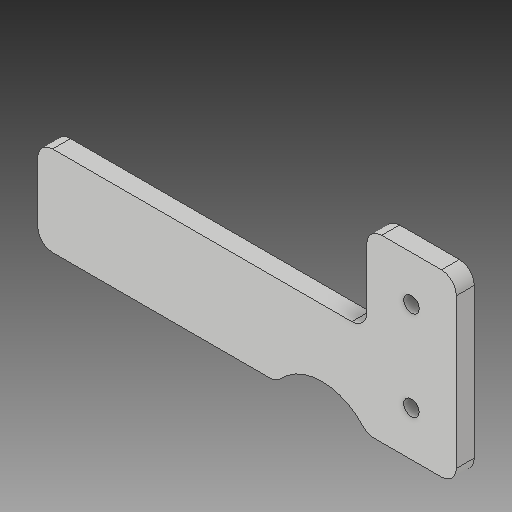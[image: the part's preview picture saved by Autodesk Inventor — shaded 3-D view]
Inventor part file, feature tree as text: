
AUTODESK INVENTOR PART (.ipt)
format: ipt  version: 2018 (Build 220112000, 112)  size: 117,760 bytes
history: native  units: mm
features: other x3, sketch x1
ambient origin geometry x8: Origin, YZ Plane, XZ Plane, XY Plane, X Axis, Y Axis, Z Axis, Center Point
bodies: Solid1 (feature_tree)
feature tree (4):
  other  "Spool Holder.ipt"
  other  "Solid1::Spool Holder.ipt"
  other  "TaggingFeature1"
  sketch  "Sketch1"  dims[d0=10.0mm]
